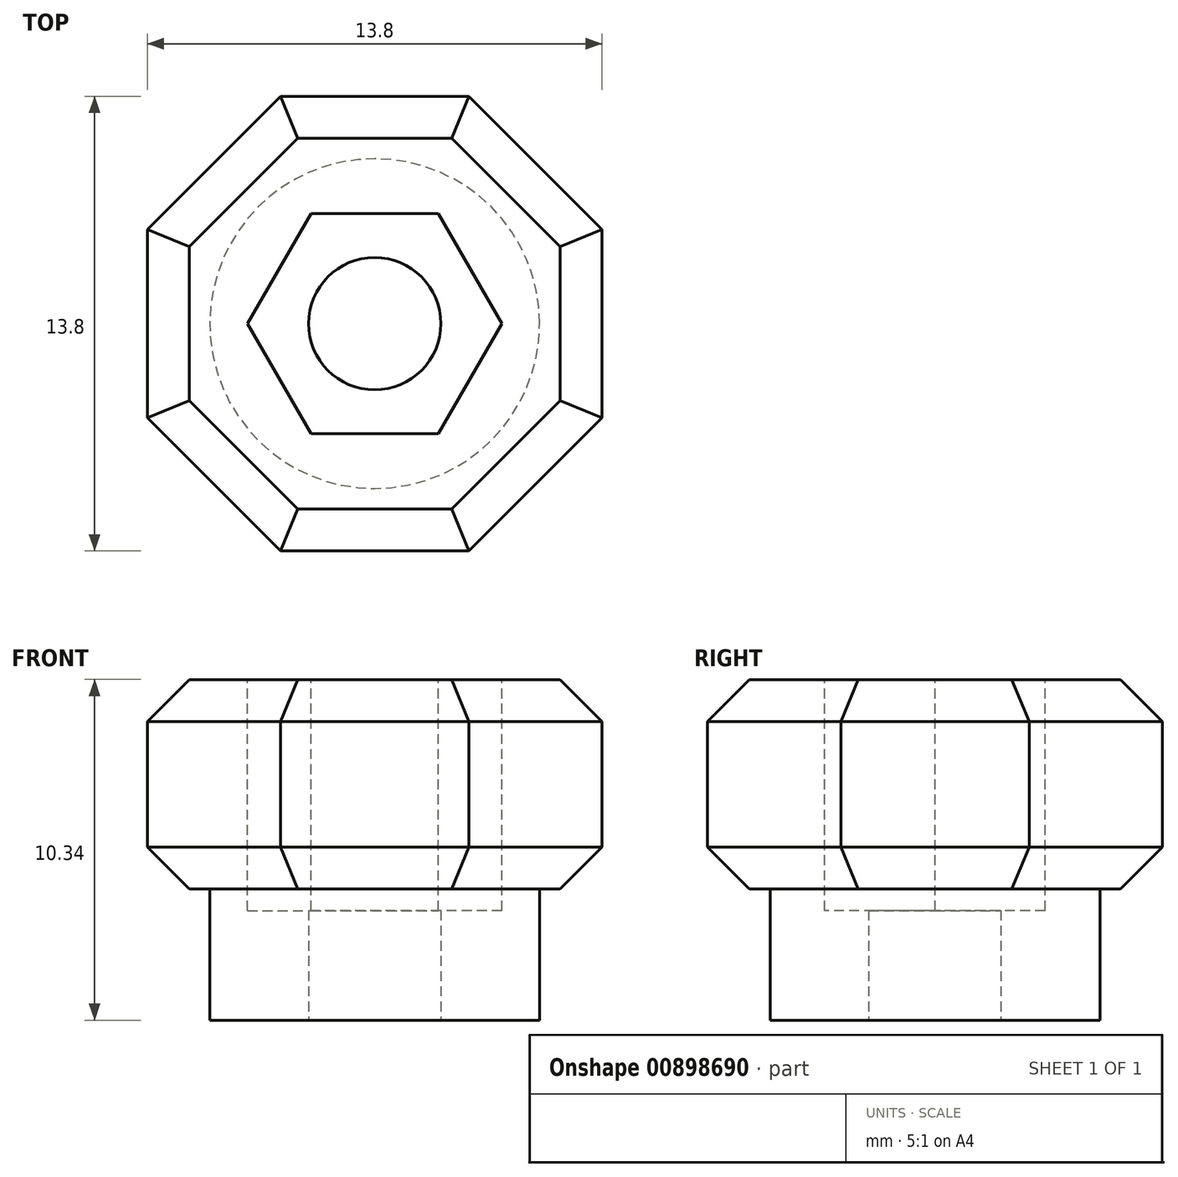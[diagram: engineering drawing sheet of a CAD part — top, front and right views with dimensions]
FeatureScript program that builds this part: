
annotation { "Feature Type Name" : "Feature", "Feature Type Description" : "" }
export const myFeature = defineFeature(function(context is Context, id is Id, definition is map)
    precondition{}
    {
        {
            var Q0;
            Q0=qCreatedBy(makeId("Top.planeOp"),FACE);
            var sketch = newSketch(context, id + "F0", { "sketchPlane" : qUnion([Q0])});
            skCircle(sketch, "E0", {"center": v(0, 0) * mm, "radius": 2 * mm});
            skCircle(sketch, "E1", {"center": v(0, 0) * mm, "radius": 5 * mm});
            skSolve(sketch);
        }
        {
            var Q0;
            Q0=makeQuery(id+"F0.imprint","IMPRINT",FACE,{"disambiguationData":[TD([[makeQuery(id+"F0.imprint","IMPRINT",EDGE,{"derivedFrom":sQuery(id+"F0.wireOp",EDGE,"E0")}),-1.0]])]});
            extrude(context, id + "F1", {"entities" : qUnion([Q0]), "depth" : 4 * mm, "offsetDistance" : 25.4 * mm});
        }
        {
            var Q0;
            Q0=makeQuery(id+"F1.opExtrude","CAP_FACE",FACE,{"disambiguationData":[OSD([sQuery(id+"F0.wireOp",EDGE,"E0"),sQuery(id+"F0.wireOp",EDGE,"E1")])],"isStart":false});
            var sketch = newSketch(context, id + "F2", { "sketchPlane" : qUnion([Q0])});
            skCircle(sketch, "E2.cCircle", {"center": v(0, 0) * mm, "radius": 7.47 * mm, "construction": true});
            skLineSegment(sketch, "E2.0", {"start": v(2.86, -6.9) * mm, "end": v(-2.86, -6.9) * mm});
            skLineSegment(sketch, "E2.1", {"start": v(-2.86, -6.9) * mm, "end": v(-6.9, -2.86) * mm});
            skLineSegment(sketch, "E2.2", {"start": v(-6.9, -2.86) * mm, "end": v(-6.9, 2.86) * mm});
            skLineSegment(sketch, "E2.3", {"start": v(-6.9, 2.86) * mm, "end": v(-2.86, 6.9) * mm});
            skLineSegment(sketch, "E2.4", {"start": v(-2.86, 6.9) * mm, "end": v(2.86, 6.9) * mm});
            skLineSegment(sketch, "E2.5", {"start": v(2.86, 6.9) * mm, "end": v(6.9, 2.86) * mm});
            skLineSegment(sketch, "E2.6", {"start": v(6.9, 2.86) * mm, "end": v(6.9, -2.86) * mm});
            skLineSegment(sketch, "E2.7", {"start": v(6.9, -2.86) * mm, "end": v(2.86, -6.9) * mm});
            skSolve(sketch);
        }
        {
            var Q0;
            Q0=makeQuery(id+"F2.imprint","IMPRINT",FACE,{"disambiguationData":[TD([[makeQuery(id+"F2.imprint","IMPRINT",EDGE,{"derivedFrom":sQuery(id+"F2.wireOp",EDGE,"E2.0")}),-1.0]])]});
            var Q1;
            Q1=makeQuery(id+"F2.imprint","IMPRINT",FACE,{"disambiguationData":[TD([[makeQuery(id+"F2.imprint","IMPRINT",EDGE,{"derivedFrom":makeQuery(id+"F1.opExtrude","CAP_EDGE",EDGE,{"disambiguationData":[OSD([sQuery(id+"F0.wireOp",EDGE,"E0")])],"isStart":false})}),-1.0]])]});
            extrude(context, id + "F3", {"entities" : qUnion([Q0, Q1]), "operationType" : NewBodyOperationType.ADD, "depth" : 6.35 * mm, "offsetDistance" : 25.4 * mm});
        }
        {
            var Q0;
            Q0=makeQuery(id+"F3.opExtrude","CAP_EDGE",EDGE,{"disambiguationData":[OSD([sQuery(id+"F2.wireOp",EDGE,"E2.2")])],"isStart":false});
            var Q1;
            Q1=makeQuery(id+"F3.opExtrude","CAP_EDGE",EDGE,{"disambiguationData":[OSD([sQuery(id+"F2.wireOp",EDGE,"E2.3")])],"isStart":false});
            var Q2;
            Q2=makeQuery(id+"F3.opExtrude","CAP_EDGE",EDGE,{"disambiguationData":[OSD([sQuery(id+"F2.wireOp",EDGE,"E2.4")])],"isStart":false});
            var Q3;
            Q3=makeQuery(id+"F3.opExtrude","CAP_EDGE",EDGE,{"disambiguationData":[OSD([sQuery(id+"F2.wireOp",EDGE,"E2.5")])],"isStart":false});
            var Q4;
            Q4=makeQuery(id+"F3.opExtrude","CAP_EDGE",EDGE,{"disambiguationData":[OSD([sQuery(id+"F2.wireOp",EDGE,"E2.6")])],"isStart":false});
            var Q5;
            Q5=makeQuery(id+"F3.opExtrude","CAP_EDGE",EDGE,{"disambiguationData":[OSD([sQuery(id+"F2.wireOp",EDGE,"E2.7")])],"isStart":false});
            var Q6;
            Q6=makeQuery(id+"F3.opExtrude","CAP_EDGE",EDGE,{"disambiguationData":[OSD([sQuery(id+"F2.wireOp",EDGE,"E2.0")])],"isStart":false});
            var Q7;
            Q7=makeQuery(id+"F3.opExtrude","CAP_EDGE",EDGE,{"disambiguationData":[OSD([sQuery(id+"F2.wireOp",EDGE,"E2.1")])],"isStart":false});
            var Q8;
            Q8=makeQuery(id+"F3.opExtrude","CAP_EDGE",EDGE,{"disambiguationData":[OSD([sQuery(id+"F2.wireOp",EDGE,"E2.0")])],"isStart":true});
            var Q9;
            Q9=makeQuery(id+"F3.opExtrude","CAP_EDGE",EDGE,{"disambiguationData":[OSD([sQuery(id+"F2.wireOp",EDGE,"E2.1")])],"isStart":true});
            var Q10;
            Q10=makeQuery(id+"F3.opExtrude","CAP_EDGE",EDGE,{"disambiguationData":[OSD([sQuery(id+"F2.wireOp",EDGE,"E2.7")])],"isStart":true});
            var Q11;
            Q11=makeQuery(id+"F3.opExtrude","CAP_EDGE",EDGE,{"disambiguationData":[OSD([sQuery(id+"F2.wireOp",EDGE,"E2.2")])],"isStart":true});
            var Q12;
            Q12=makeQuery(id+"F3.opExtrude","CAP_EDGE",EDGE,{"disambiguationData":[OSD([sQuery(id+"F2.wireOp",EDGE,"E2.6")])],"isStart":true});
            var Q13;
            Q13=makeQuery(id+"F3.opExtrude","CAP_EDGE",EDGE,{"disambiguationData":[OSD([sQuery(id+"F2.wireOp",EDGE,"E2.5")])],"isStart":true});
            var Q14;
            Q14=makeQuery(id+"F3.opExtrude","CAP_EDGE",EDGE,{"disambiguationData":[OSD([sQuery(id+"F2.wireOp",EDGE,"E2.4")])],"isStart":true});
            var Q15;
            Q15=makeQuery(id+"F3.opExtrude","CAP_EDGE",EDGE,{"disambiguationData":[OSD([sQuery(id+"F2.wireOp",EDGE,"E2.3")])],"isStart":true});
            chamfer(context, id + "F4", {"entities" : qUnion([Q0, Q1, Q2, Q3, Q4, Q5, Q6, Q7, Q8, Q9, Q10, Q11, Q12, Q13, Q14, Q15]), "width" : 1.27 * mm, "tangentPropagation" : true});
        }
        {
            var Q0;
            Q0=makeQuery(id+"F3.opExtrude","CAP_FACE",FACE,{"disambiguationData":[OSD([sQuery(id+"F0.wireOp",EDGE,"E0"),sQuery(id+"F2.wireOp",EDGE,"E2.0"),sQuery(id+"F2.wireOp",EDGE,"E2.1"),sQuery(id+"F2.wireOp",EDGE,"E2.2"),sQuery(id+"F2.wireOp",EDGE,"E2.3"),sQuery(id+"F2.wireOp",EDGE,"E2.4"),sQuery(id+"F2.wireOp",EDGE,"E2.5"),sQuery(id+"F2.wireOp",EDGE,"E2.6"),sQuery(id+"F2.wireOp",EDGE,"E2.7")])],"isStart":false});
            var sketch = newSketch(context, id + "F5", { "sketchPlane" : qUnion([Q0])});
            skCircle(sketch, "E3.cCircle", {"center": v(0, 0) * mm, "radius": 3.86 * mm, "construction": true});
            skLineSegment(sketch, "E3.0", {"start": v(3.86, 0) * mm, "end": v(1.93, -3.34) * mm});
            skLineSegment(sketch, "E3.1", {"start": v(1.93, -3.34) * mm, "end": v(-1.93, -3.34) * mm});
            skLineSegment(sketch, "E3.2", {"start": v(-1.93, -3.34) * mm, "end": v(-3.86, 0) * mm});
            skLineSegment(sketch, "E3.3", {"start": v(-3.86, 0) * mm, "end": v(-1.93, 3.34) * mm});
            skLineSegment(sketch, "E3.4", {"start": v(-1.93, 3.34) * mm, "end": v(1.93, 3.34) * mm});
            skLineSegment(sketch, "E3.5", {"start": v(1.93, 3.34) * mm, "end": v(3.86, 0) * mm});
            skSolve(sketch);
        }
        {
            var Q0;
            Q0=qSketchRegion(id+"F5",true);
            extrude(context, id + "F6", {"entities" : qUnion([Q0]), "operationType" : NewBodyOperationType.REMOVE, "oppositeDirection" : true, "depth" : 7 * mm, "offsetDistance" : 25.4 * mm});
        }
    });
